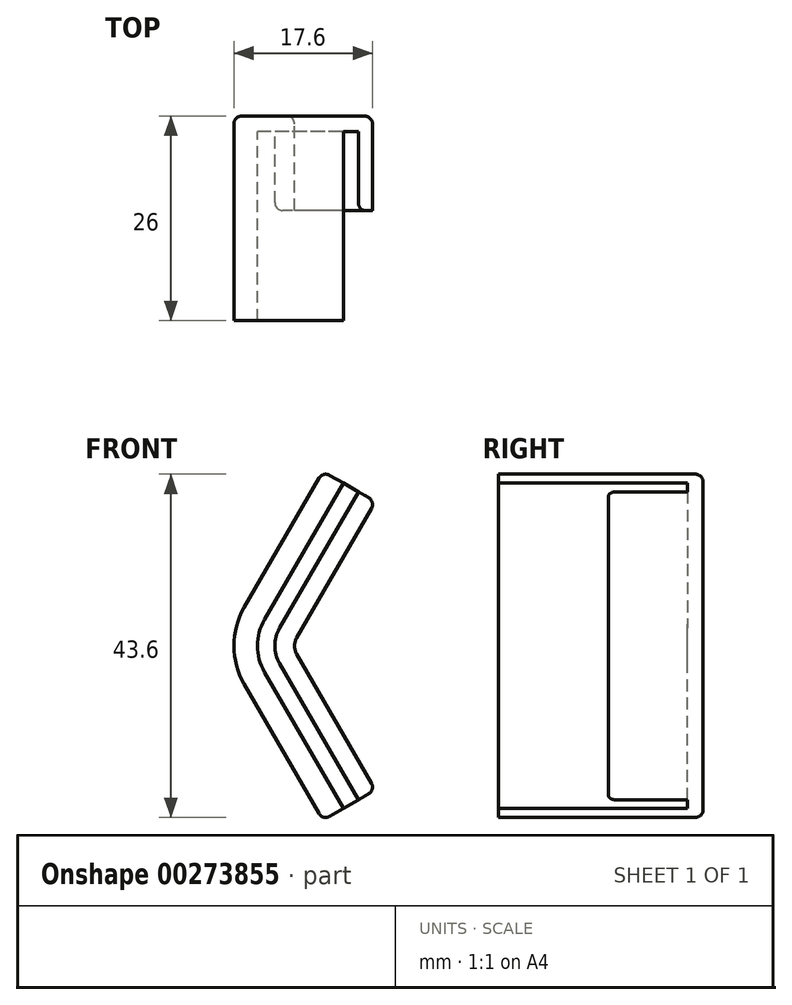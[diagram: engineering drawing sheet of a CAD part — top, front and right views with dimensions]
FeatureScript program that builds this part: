
annotation { "Feature Type Name" : "Feature", "Feature Type Description" : "" }
export const myFeature = defineFeature(function(context is Context, id is Id, definition is map)
    precondition{}
    {
        {
            var Q0;
            Q0=qCreatedBy(makeId("Top.planeOp"),FACE);
            var sketch = newSketch(context, id + "F0", { "sketchPlane" : qUnion([Q0])});
            skLineSegment(sketch, "E0.bottom", {"start": v(-9.7, 15.21) * mm, "end": v(-6.7, 15.21) * mm});
            skLineSegment(sketch, "E0.top", {"start": v(-9.7, -10.79) * mm, "end": v(-6.7, -10.79) * mm});
            skLineSegment(sketch, "E0.left", {"start": v(-9.7, 15.21) * mm, "end": v(-9.7, -10.79) * mm});
            skLineSegment(sketch, "E0.right", {"start": v(-6.7, 13.21) * mm, "end": v(-6.7, -10.79) * mm});
            skLineSegment(sketch, "E1.bottom", {"start": v(-6.7, 15.21) * mm, "end": v(-2, 15.21) * mm});
            skLineSegment(sketch, "E1.top", {"start": v(-6.7, 13.21) * mm, "end": v(-4.5, 13.21) * mm});
            skLineSegment(sketch, "E1.right", {"start": v(-2, 15.21) * mm, "end": v(-2, 13.21) * mm});
            skLineSegment(sketch, "E2.bottom", {"start": v(-2, 3.21) * mm, "end": v(-4.5, 3.21) * mm});
            skLineSegment(sketch, "E2.left", {"start": v(-2, 3.21) * mm, "end": v(-2, 13.21) * mm});
            skLineSegment(sketch, "E2.right", {"start": v(-4.5, 3.21) * mm, "end": v(-4.5, 13.21) * mm});
            skLineSegment(sketch, "E3", {"start": v(0, 25.92) * mm, "end": v(0, -17.65) * mm, "construction": true});
            skSolve(sketch);
        }
        {
            var Q0;
            Q0=makeQuery(id+"F0.imprint","IMPRINT",FACE,{"disambiguationData":[TD([[makeQuery(id+"F0.imprint","IMPRINT",EDGE,{"derivedFrom":sQuery(id+"F0.wireOp",EDGE,"E0.bottom")}),-1.0]])]});
            var Q1;
            Q1=sQuery(id+"F0.wireOp",EDGE,"E3");
            revolve(context, id + "F1", {"entities" : qUnion([Q0]), "axis" : qUnion([Q1]), "revolveType" : RevolveType.SYMMETRIC, "angle" : 60 * degree});
        }
        {
            var Q0;
            Q0=makeQuery(id+"F1.opRevolve","CAP_FACE",FACE,{"disambiguationData":[OSD([sQuery(id+"F0.wireOp",EDGE,"E0.bottom"),sQuery(id+"F0.wireOp",EDGE,"E0.top"),sQuery(id+"F0.wireOp",EDGE,"E0.left"),sQuery(id+"F0.wireOp",EDGE,"E0.right"),sQuery(id+"F0.wireOp",EDGE,"E1.bottom"),sQuery(id+"F0.wireOp",EDGE,"E1.top"),sQuery(id+"F0.wireOp",EDGE,"E1.right"),sQuery(id+"F0.wireOp",EDGE,"E2.bottom"),sQuery(id+"F0.wireOp",EDGE,"E2.left"),sQuery(id+"F0.wireOp",EDGE,"E2.right")])],"isStart":true});
            var sketch = newSketch(context, id + "F2", { "sketchPlane" : qUnion([Q0])});
            skLineSegment(sketch, "E4", {"start": v(-9.7, 15.21) * mm, "end": v(-2, 15.21) * mm});
            skLineSegment(sketch, "E5", {"start": v(-2, 15.21) * mm, "end": v(-2, 3.21) * mm});
            skLineSegment(sketch, "E6", {"start": v(-2, 3.21) * mm, "end": v(-4.5, 3.21) * mm});
            skLineSegment(sketch, "E7", {"start": v(-4.5, 3.21) * mm, "end": v(-4.5, 13.21) * mm});
            skLineSegment(sketch, "E8", {"start": v(-4.5, 13.21) * mm, "end": v(-6.7, 13.21) * mm});
            skLineSegment(sketch, "E9", {"start": v(-6.7, 13.21) * mm, "end": v(-6.7, -10.79) * mm});
            skLineSegment(sketch, "E10", {"start": v(-6.7, -10.79) * mm, "end": v(-9.7, -10.79) * mm});
            skLineSegment(sketch, "E11", {"start": v(-9.7, -10.79) * mm, "end": v(-9.7, 15.21) * mm});
            skSolve(sketch);
        }
        {
            var Q0;
            Q0=makeQuery(id+"F2.imprint","IMPRINT",FACE,{"disambiguationData":[TD([[makeQuery(id+"F2.imprint","IMPRINT",EDGE,{"derivedFrom":sQuery(id+"F2.wireOp",EDGE,"E4")}),-1.0]])]});
            extrude(context, id + "F3", {"entities" : qUnion([Q0]), "operationType" : NewBodyOperationType.ADD, "depth" : 20 * mm});
        }
        {
            var Q0;
            Q0=makeQuery(id+"F1.opRevolve","CAP_FACE",FACE,{"disambiguationData":[OSD([sQuery(id+"F0.wireOp",EDGE,"E0.bottom"),sQuery(id+"F0.wireOp",EDGE,"E0.top"),sQuery(id+"F0.wireOp",EDGE,"E0.left"),sQuery(id+"F0.wireOp",EDGE,"E0.right"),sQuery(id+"F0.wireOp",EDGE,"E1.bottom"),sQuery(id+"F0.wireOp",EDGE,"E1.top"),sQuery(id+"F0.wireOp",EDGE,"E1.right"),sQuery(id+"F0.wireOp",EDGE,"E2.bottom"),sQuery(id+"F0.wireOp",EDGE,"E2.left"),sQuery(id+"F0.wireOp",EDGE,"E2.right")])],"isStart":false});
            var sketch = newSketch(context, id + "F4", { "sketchPlane" : qUnion([Q0])});
            skLineSegment(sketch, "E12", {"start": v(-2, -3.21) * mm, "end": v(-2, -15.21) * mm});
            skLineSegment(sketch, "E13", {"start": v(-2, -15.21) * mm, "end": v(-9.7, -15.21) * mm});
            skLineSegment(sketch, "E14", {"start": v(-9.7, -15.21) * mm, "end": v(-9.7, 10.79) * mm});
            skLineSegment(sketch, "E15", {"start": v(-9.7, 10.79) * mm, "end": v(-6.7, 10.79) * mm});
            skLineSegment(sketch, "E16", {"start": v(-6.7, 10.79) * mm, "end": v(-6.7, -13.21) * mm});
            skLineSegment(sketch, "E17", {"start": v(-6.7, -13.21) * mm, "end": v(-4.5, -13.21) * mm});
            skLineSegment(sketch, "E18", {"start": v(-4.5, -13.21) * mm, "end": v(-4.5, -3.21) * mm});
            skLineSegment(sketch, "E19", {"start": v(-4.5, -3.21) * mm, "end": v(-2, -3.21) * mm});
            skSolve(sketch);
        }
        {
            var Q0;
            Q0 = qSketchRegion(id + "F4", true);
            extrude(context, id + "F5", {"entities" : qUnion([Q0]), "operationType" : NewBodyOperationType.ADD, "depth" : 20 * mm});
        }
        {
            var Q0;
            Q0=makeQuery(id+"F3.opExtrude","SWEPT_EDGE",EDGE,{"disambiguationData":[OSD([sQuery(id+"F2.wireOp",EDGE,"E6"),sQuery(id+"F2.wireOp",EDGE,"E7")])]});
            var Q1;
            Q1=makeQuery(id+"F5.opExtrude","SWEPT_EDGE",EDGE,{"disambiguationData":[OSD([sQuery(id+"F4.wireOp",EDGE,"E13"),sQuery(id+"F4.wireOp",EDGE,"E14")])]});
            fillet(context, id + "F6", {"entities" : qUnion([Q0, Q1]), "radius" : 1 * mm, "tangentPropagation" : true, "allowEdgeOverflow" : false});
        }
        {
            var Q0;
            Q0=makeQuery(id+"F5.opExtrude","SWEPT_EDGE",EDGE,{"disambiguationData":[OSD([sQuery(id+"F4.wireOp",EDGE,"E12"),sQuery(id+"F4.wireOp",EDGE,"E13")])]});
            fillet(context, id + "F7", {"entities" : qUnion([Q0]), "radius" : 1 * mm, "tangentPropagation" : true, "allowEdgeOverflow" : false});
        }
        {
            var Q0;
            Q0=makeQuery(id+"F3.opExtrude","CAP_EDGE",EDGE,{"disambiguationData":[OSD([sQuery(id+"F2.wireOp",EDGE,"E4")])],"isStart":false});
            fillet(context, id + "F8", {"entities" : qUnion([Q0]), "radius" : 1 * mm, "tangentPropagation" : true, "allowEdgeOverflow" : false});
        }
        {
            var Q0;
            Q0=makeQuery(id+"F5.opExtrude","CAP_EDGE",EDGE,{"disambiguationData":[OSD([sQuery(id+"F4.wireOp",EDGE,"E14")])],"isStart":false});
            fillet(context, id + "F9", {"entities" : qUnion([Q0]), "radius" : 1 * mm, "tangentPropagation" : true, "allowEdgeOverflow" : false});
        }
    });
